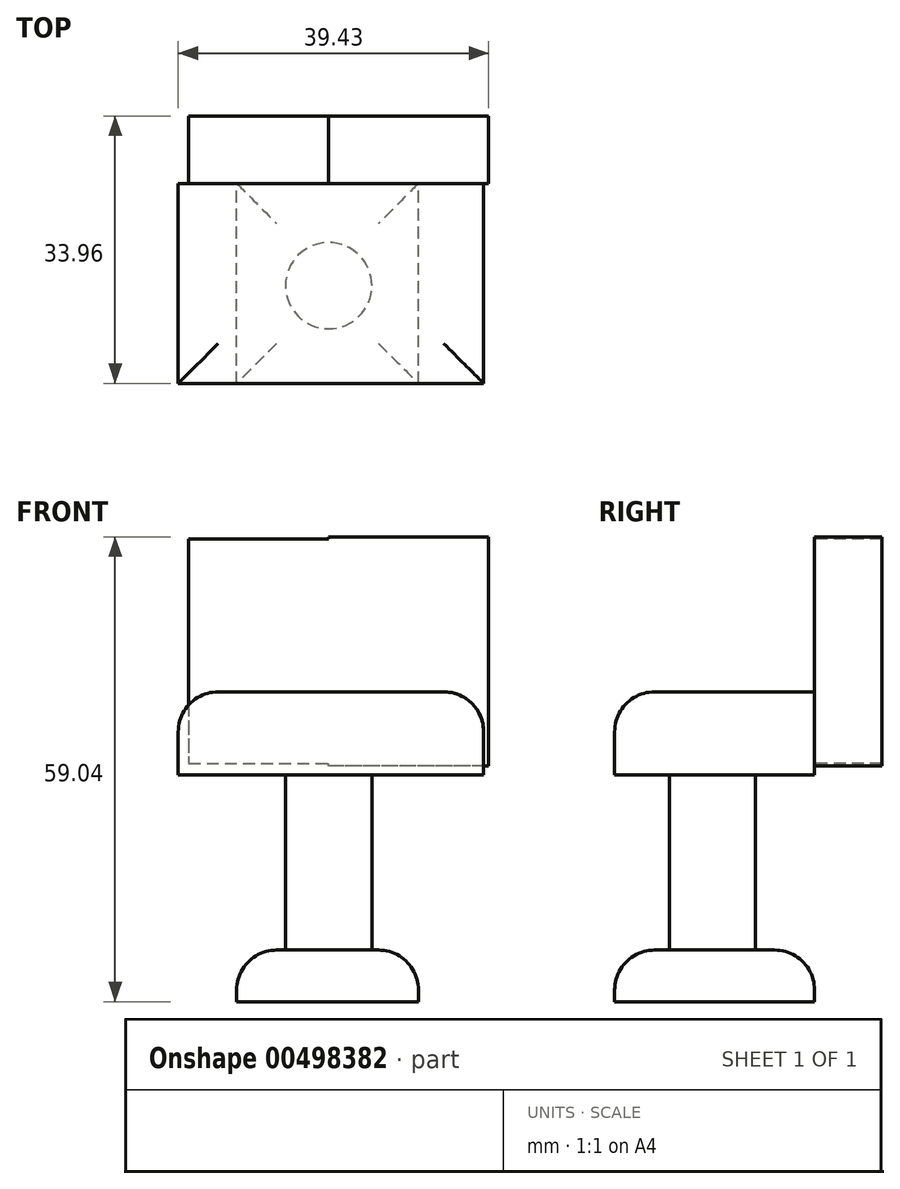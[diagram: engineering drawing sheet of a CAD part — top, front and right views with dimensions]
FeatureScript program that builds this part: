
annotation { "Feature Type Name" : "Feature", "Feature Type Description" : "" }
export const myFeature = defineFeature(function(context is Context, id is Id, definition is map)
    precondition{}
    {
        {
            var Q0;
            Q0=qCreatedBy(makeId("Front.planeOp"),FACE);
            var sketch = newSketch(context, id + "F0", { "sketchPlane" : qUnion([Q0])});
            skLineSegment(sketch, "E0.bottom", {"start": v(-19.11, 5) * mm, "end": v(19.68, 5) * mm});
            skLineSegment(sketch, "E0.top", {"start": v(-19.11, -5.56) * mm, "end": v(19.68, -5.56) * mm});
            skLineSegment(sketch, "E0.left", {"start": v(-19.11, 5) * mm, "end": v(-19.11, -5.56) * mm});
            skLineSegment(sketch, "E0.right", {"start": v(19.68, 5) * mm, "end": v(19.68, -5.56) * mm});
            skSolve(sketch);
        }
        {
            var Q0;
            Q0=qSketchRegion(id+"F0",true);
            extrude(context, id + "F1", {"entities" : qUnion([Q0]), "depth" : 25.4 * mm});
        }
        {
            var Q0;
            Q0=qCreatedBy(makeId("Right.planeOp"),FACE);
            var sketch = newSketch(context, id + "F2", { "sketchPlane" : qUnion([Q0])});
            skLineSegment(sketch, "E1.bottom", {"start": v(0, -4.42) * mm, "end": v(8.56, -4.42) * mm});
            skLineSegment(sketch, "E1.top", {"start": v(0, 24.67) * mm, "end": v(8.56, 24.67) * mm});
            skLineSegment(sketch, "E1.left", {"start": v(0, -4.42) * mm, "end": v(0, 24.67) * mm});
            skLineSegment(sketch, "E1.right", {"start": v(8.56, -4.42) * mm, "end": v(8.56, 24.67) * mm});
            skSolve(sketch);
        }
        {
            var Q0;
            Q0=qSketchRegion(id+"F2",true);
            extrude(context, id + "F3", {"entities" : qUnion([Q0]), "operationType" : NewBodyOperationType.ADD, "depth" : 20.32 * mm});
        }
        {
            var Q0;
            Q0=qCreatedBy(makeId("Right.planeOp"),FACE);
            var sketch = newSketch(context, id + "F4", { "sketchPlane" : qUnion([Q0])});
            skLineSegment(sketch, "E2.bottom", {"start": v(8.56, 24.39) * mm, "end": v(0, 24.39) * mm});
            skLineSegment(sketch, "E2.top", {"start": v(8.56, -4.14) * mm, "end": v(0, -4.14) * mm});
            skLineSegment(sketch, "E2.left", {"start": v(8.56, 24.39) * mm, "end": v(8.56, -4.14) * mm});
            skLineSegment(sketch, "E2.right", {"start": v(0, 24.39) * mm, "end": v(0, -4.14) * mm});
            skSolve(sketch);
        }
        {
            var Q0;
            Q0=qSketchRegion(id+"F4",true);
            extrude(context, id + "F5", {"entities" : qUnion([Q0]), "operationType" : NewBodyOperationType.ADD, "oppositeDirection" : true, "depth" : 17.78 * mm});
        }
        {
            var Q0;
            Q0=qCreatedBy(makeId("Top.planeOp"),FACE);
            var sketch = newSketch(context, id + "F6", { "sketchPlane" : qUnion([Q0])});
            skCircle(sketch, "E3", {"center": v(0, -12.98) * mm, "radius": 5.48 * mm});
            skSolve(sketch);
        }
        {
            var Q0;
            Q0=qSketchRegion(id+"F6",true);
            extrude(context, id + "F7", {"entities" : qUnion([Q0]), "operationType" : NewBodyOperationType.ADD, "oppositeDirection" : true, "depth" : 27.94 * mm});
        }
        {
            var Q0;
            Q0=qCreatedBy(makeId("Front.planeOp"),FACE);
            var sketch = newSketch(context, id + "F8", { "sketchPlane" : qUnion([Q0])});
            skLineSegment(sketch, "E4.bottom", {"start": v(-11.7, -34.37) * mm, "end": v(11.4, -34.37) * mm});
            skLineSegment(sketch, "E4.top", {"start": v(-11.7, -27.81) * mm, "end": v(11.4, -27.81) * mm});
            skLineSegment(sketch, "E4.left", {"start": v(-11.7, -34.37) * mm, "end": v(-11.7, -27.81) * mm});
            skLineSegment(sketch, "E4.right", {"start": v(11.4, -34.37) * mm, "end": v(11.4, -27.81) * mm});
            skSolve(sketch);
        }
        {
            var Q0;
            Q0=qSketchRegion(id+"F8",true);
            extrude(context, id + "F9", {"entities" : qUnion([Q0]), "operationType" : NewBodyOperationType.ADD, "depth" : 25.4 * mm});
        }
        {
            var Q0;
            Q0=makeQuery(id+"F1.opExtrude","CAP_EDGE",EDGE,{"disambiguationData":[OSD([sQuery(id+"F0.wireOp",EDGE,"E0.bottom")])],"isStart":false});
            var Q1;
            Q1=makeQuery(id+"F1.opExtrude","SWEPT_EDGE",EDGE,{"disambiguationData":[OSD([sQuery(id+"F0.wireOp",EDGE,"E0.bottom"),sQuery(id+"F0.wireOp",EDGE,"E0.left")])]});
            var Q2;
            Q2=makeQuery(id+"F1.opExtrude","SWEPT_EDGE",EDGE,{"disambiguationData":[OSD([sQuery(id+"F0.wireOp",EDGE,"E0.bottom"),sQuery(id+"F0.wireOp",EDGE,"E0.right")])]});
            var Q3;
            Q3=makeQuery(id+"F9.opExtrude","CAP_EDGE",EDGE,{"disambiguationData":[OSD([sQuery(id+"F8.wireOp",EDGE,"E4.top")])],"isStart":false});
            var Q4;
            Q4=makeQuery(id+"F9.opExtrude","SWEPT_EDGE",EDGE,{"disambiguationData":[OSD([sQuery(id+"F8.wireOp",EDGE,"E4.top"),sQuery(id+"F8.wireOp",EDGE,"E4.right")])]});
            var Q5;
            Q5=makeQuery(id+"F9.opExtrude","SWEPT_EDGE",EDGE,{"disambiguationData":[OSD([sQuery(id+"F8.wireOp",EDGE,"E4.top"),sQuery(id+"F8.wireOp",EDGE,"E4.left")])]});
            var Q6;
            Q6=makeQuery(id+"F9.opExtrude","CAP_EDGE",EDGE,{"disambiguationData":[OSD([sQuery(id+"F8.wireOp",EDGE,"E4.top")])],"isStart":true});
            fillet(context, id + "F10", {"entities" : qUnion([Q0, Q1, Q2, Q3, Q4, Q5, Q6]), "radius" : 5.08 * mm, "tangentPropagation" : true, "allowEdgeOverflow" : false});
        }
    });
